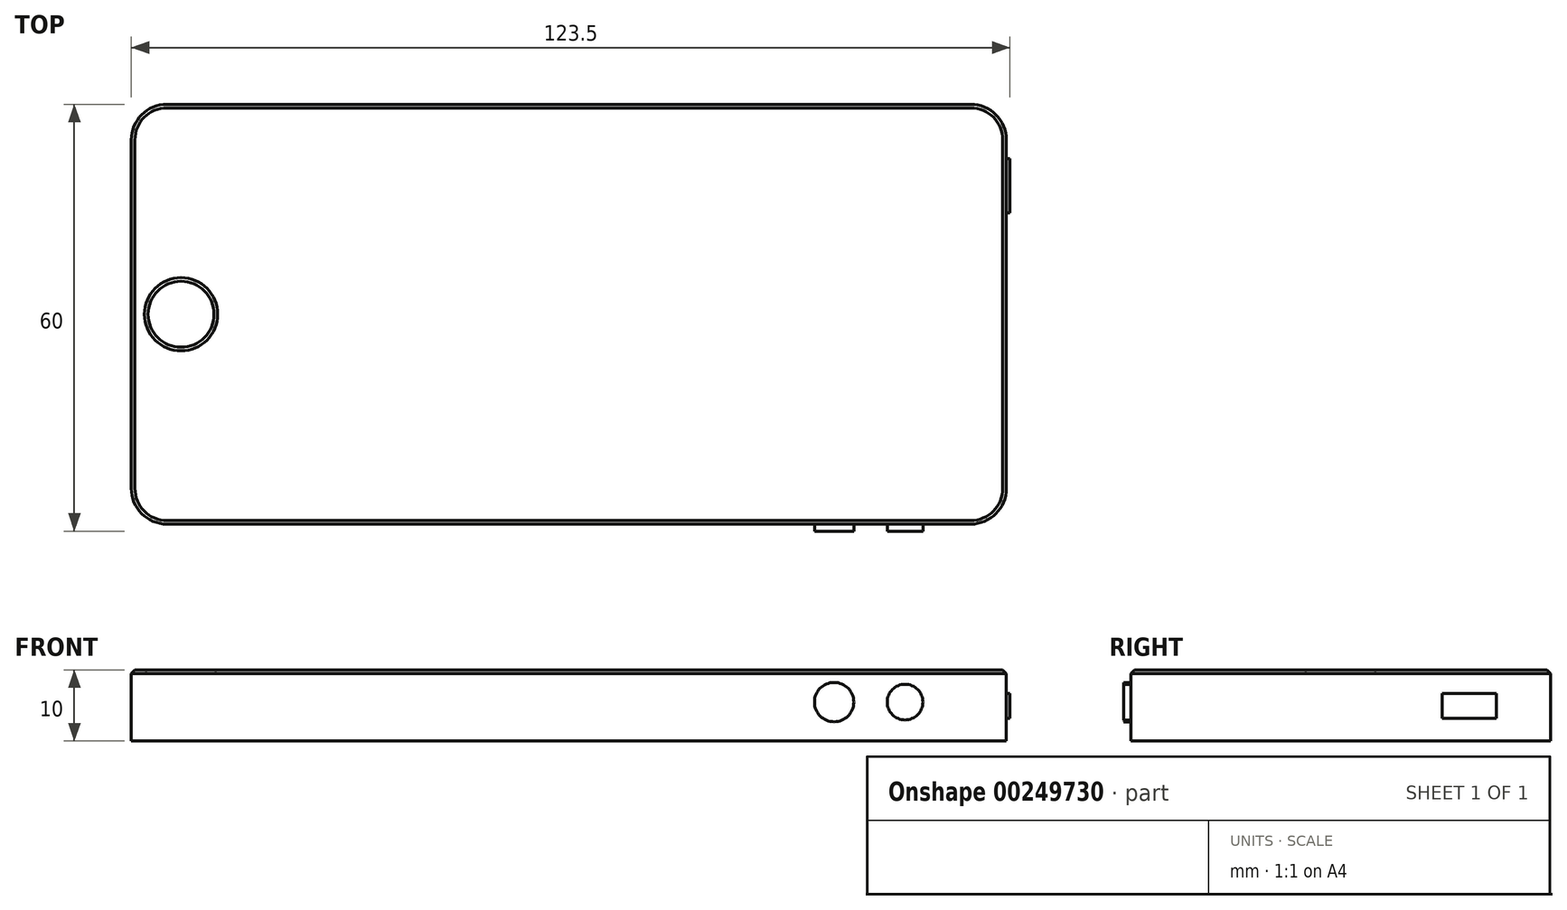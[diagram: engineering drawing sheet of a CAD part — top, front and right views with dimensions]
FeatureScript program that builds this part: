
annotation { "Feature Type Name" : "Feature", "Feature Type Description" : "" }
export const myFeature = defineFeature(function(context is Context, id is Id, definition is map)
    precondition{}
    {
        {
            var Q0;
            Q0=qCreatedBy(makeId("Top.planeOp"),FACE);
            var sketch = newSketch(context, id + "F0", { "sketchPlane" : qUnion([Q0])});
            skLineSegment(sketch, "E0.bottom", {"start": v(-61.5, 29.5) * mm, "end": v(61.5, 29.5) * mm});
            skLineSegment(sketch, "E0.top", {"start": v(-61.5, -29.5) * mm, "end": v(61.5, -29.5) * mm});
            skLineSegment(sketch, "E0.left", {"start": v(-61.5, 29.5) * mm, "end": v(-61.5, -29.5) * mm});
            skLineSegment(sketch, "E0.right", {"start": v(61.5, 29.5) * mm, "end": v(61.5, -29.5) * mm});
            skPoint(sketch, "E0.middle", {"position": v(0, 0) * mm});
            skSolve(sketch);
        }
        {
            var Q0;
            Q0=makeQuery(id+"F0.imprint","IMPRINT",FACE,{"disambiguationData":[TD([[makeQuery(id+"F0.imprint","IMPRINT",EDGE,{"derivedFrom":sQuery(id+"F0.wireOp",EDGE,"E0.bottom")}),-1.0]])]});
            extrude(context, id + "F1", {"entities" : qUnion([Q0]), "depth" : 10 * mm});
        }
        {
            var Q0;
            Q0=makeQuery(id+"F1.opExtrude","SWEPT_EDGE",EDGE,{"disambiguationData":[OSD([sQuery(id+"F0.wireOp",EDGE,"E0.bottom"),sQuery(id+"F0.wireOp",EDGE,"E0.left")])]});
            var Q1;
            Q1=makeQuery(id+"F1.opExtrude","SWEPT_EDGE",EDGE,{"disambiguationData":[OSD([sQuery(id+"F0.wireOp",EDGE,"E0.bottom"),sQuery(id+"F0.wireOp",EDGE,"E0.right")])]});
            fillet(context, id + "F2", {"entities" : qUnion([Q0, Q1]), "radius" : 5 * mm, "tangentPropagation" : true, "allowEdgeOverflow" : false});
        }
        {
            var Q0;
            Q0=makeQuery(id+"F1.opExtrude","SWEPT_EDGE",EDGE,{"disambiguationData":[OSD([sQuery(id+"F0.wireOp",EDGE,"E0.top"),sQuery(id+"F0.wireOp",EDGE,"E0.left")])]});
            var Q1;
            Q1=makeQuery(id+"F1.opExtrude","SWEPT_EDGE",EDGE,{"disambiguationData":[OSD([sQuery(id+"F0.wireOp",EDGE,"E0.top"),sQuery(id+"F0.wireOp",EDGE,"E0.right")])]});
            fillet(context, id + "F3", {"entities" : qUnion([Q0, Q1]), "radius" : 5 * mm, "tangentPropagation" : true, "allowEdgeOverflow" : false});
        }
        {
            var Q0;
            Q0=makeQuery(id+"F1.opExtrude","SWEPT_FACE",FACE,{"disambiguationData":[OSD([sQuery(id+"F0.wireOp",EDGE,"E0.top")])]});
            var sketch = newSketch(context, id + "F4", { "sketchPlane" : qUnion([Q0])});
            skCircle(sketch, "E1", {"center": v(47.26, 5.47) * mm, "radius": 2.5 * mm});
            skCircle(sketch, "E2", {"center": v(37.3, 5.47) * mm, "radius": 2.77 * mm});
            skSolve(sketch);
        }
        {
            var Q0;
            Q0=makeQuery(id+"F4.imprint","IMPRINT",FACE,{"disambiguationData":[TD([[makeQuery(id+"F4.imprint","IMPRINT",EDGE,{"derivedFrom":sQuery(id+"F4.wireOp",EDGE,"E2")}),1.0]])]});
            var Q1;
            Q1=makeQuery(id+"F4.imprint","IMPRINT",FACE,{"disambiguationData":[TD([[makeQuery(id+"F4.imprint","IMPRINT",EDGE,{"derivedFrom":sQuery(id+"F4.wireOp",EDGE,"E1")}),1.0]])]});
            extrude(context, id + "F5", {"entities" : qUnion([Q0, Q1]), "operationType" : NewBodyOperationType.ADD, "depth" : 1 * mm});
        }
        {
            var Q0;
            Q0=makeQuery(id+"F1.opExtrude","SWEPT_FACE",FACE,{"disambiguationData":[OSD([sQuery(id+"F0.wireOp",EDGE,"E0.right")])]});
            var sketch = newSketch(context, id + "F6", { "sketchPlane" : qUnion([Q0])});
            skLineSegment(sketch, "E3.bottom", {"start": v(21.9, 6.7) * mm, "end": v(14.27, 6.7) * mm});
            skLineSegment(sketch, "E3.top", {"start": v(21.9, 3.18) * mm, "end": v(14.27, 3.18) * mm});
            skLineSegment(sketch, "E3.left", {"start": v(21.9, 6.7) * mm, "end": v(21.9, 3.18) * mm});
            skLineSegment(sketch, "E3.right", {"start": v(14.27, 6.7) * mm, "end": v(14.27, 3.18) * mm});
            skPoint(sketch, "E3.middle", {"position": v(18.08, 4.94) * mm});
            skSolve(sketch);
        }
        {
            var Q0;
            Q0=qSketchRegion(id+"F6",true);
            extrude(context, id + "F7", {"entities" : qUnion([Q0]), "operationType" : NewBodyOperationType.ADD, "depth" : .5 * mm});
        }
        {
            var Q0;
            Q0=makeQuery(id+"F1.opExtrude","CAP_FACE",FACE,{"disambiguationData":[OSD([sQuery(id+"F0.wireOp",EDGE,"E0.bottom"),sQuery(id+"F0.wireOp",EDGE,"E0.top"),sQuery(id+"F0.wireOp",EDGE,"E0.left"),sQuery(id+"F0.wireOp",EDGE,"E0.right")])],"isStart":false});
            var sketch = newSketch(context, id + "F8", { "sketchPlane" : qUnion([Q0])});
            skCircle(sketch, "E4", {"center": v(-54.51, 0) * mm, "radius": 4.64 * mm});
            skSolve(sketch);
        }
        {
            var Q0;
            Q0=qSketchRegion(id+"F8",true);
            extrude(context, id + "F9", {"entities" : qUnion([Q0]), "operationType" : NewBodyOperationType.REMOVE, "oppositeDirection" : true, "depth" : .5 * mm});
        }
        {
            var Q0;
            Q0=makeQuery(id+"F1.opExtrude","CAP_FACE",FACE,{"disambiguationData":[OSD([sQuery(id+"F0.wireOp",EDGE,"E0.bottom"),sQuery(id+"F0.wireOp",EDGE,"E0.top"),sQuery(id+"F0.wireOp",EDGE,"E0.left"),sQuery(id+"F0.wireOp",EDGE,"E0.right")])],"isStart":false});
            chamfer(context, id + "F10", {"entities" : qUnion([Q0]), "width" : .5 * mm, "tangentPropagation" : true});
        }
    });
